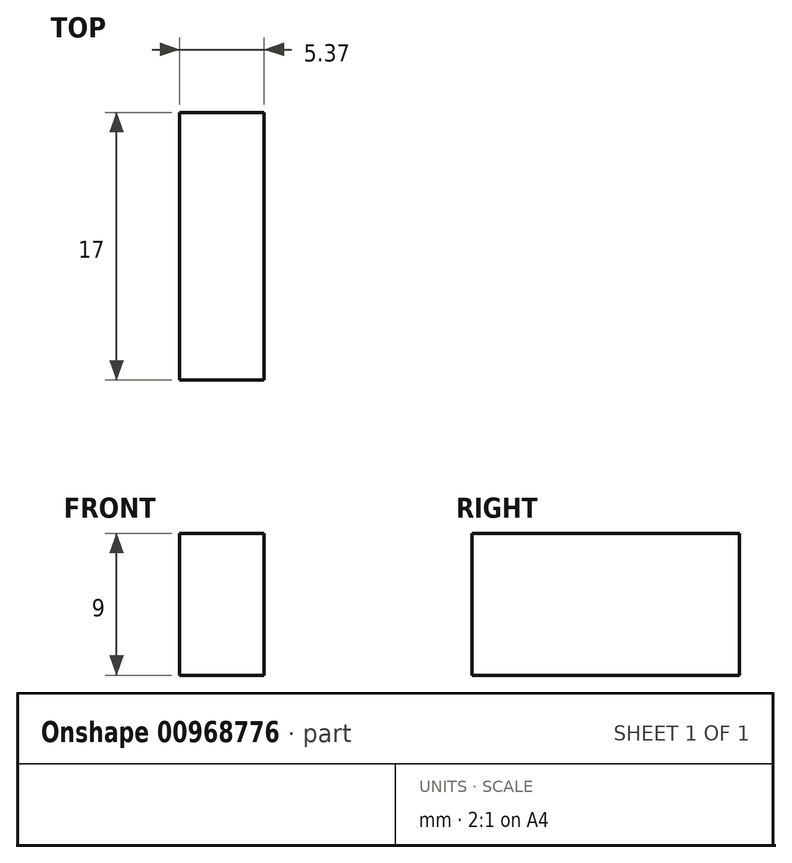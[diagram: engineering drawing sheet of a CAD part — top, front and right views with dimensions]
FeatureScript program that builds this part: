
annotation { "Feature Type Name" : "Feature", "Feature Type Description" : "" }
export const myFeature = defineFeature(function(context is Context, id is Id, definition is map)
    precondition{}
    {
        {
            var Q0;
            Q0=qCreatedBy(makeId("Top.planeOp"),FACE);
            var sketch = newSketch(context, id + "F0", { "sketchPlane" : qUnion([Q0])});
            skLineSegment(sketch, "E0.bottom", {"start": v(-18.64, 9.1) * mm, "end": v(-13.27, 9.1) * mm});
            skLineSegment(sketch, "E0.top", {"start": v(-18.64, -7.9) * mm, "end": v(-13.27, -7.9) * mm});
            skLineSegment(sketch, "E0.left", {"start": v(-18.64, 9.1) * mm, "end": v(-18.64, -7.9) * mm});
            skLineSegment(sketch, "E0.right", {"start": v(-13.27, 9.1) * mm, "end": v(-13.27, -7.9) * mm});
            skSolve(sketch);
        }
        {
            var Q0;
            Q0 = qSketchRegion(id + "F0", true);
            extrude(context, id + "F1", {"entities" : qUnion([Q0]), "endBound" : BoundingType.SYMMETRIC, "depth" : 9 * mm, "offsetDistance" : 25 * mm});
        }
    });
